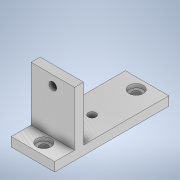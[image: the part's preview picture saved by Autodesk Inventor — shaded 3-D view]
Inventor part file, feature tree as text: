
AUTODESK INVENTOR PART (.ipt)
format: ipt  version: 2020 (Build 240168000, 168)  size: 157,696 bytes
history: native  units: mm
features: sketch x5, hole x3, extrude x2
ambient origin geometry x8: Origin, YZ Plane, XZ Plane, XY Plane, X Axis, Y Axis, Z Axis, Center Point
bodies: Body1 (feature_tree)
feature tree (10):
  extrude  "Extrusion8"  Depth=24.0mm
  hole  "Hole8"  [1 undecoded]
  extrude  "Extrusion10"  TaperAngle=0.0deg  [1 undecoded]
  hole  "Hole9"  [1 undecoded]
  hole  "Hole10"  [1 undecoded]
  sketch  "Sketch14"  dims[d93=28.0mm d94=24.0mm]
  sketch  "Sketch17"  dims[d95=16.0mm d96=5.0mm d97=0.0mm]
  sketch  "Sketch18"  dims[d111=19.0mm]
  sketch  "Sketch19"  dims[d112=4.305mm d113=6.0mm d114=7.938mm d115=2.0mm d116=14.3117mm d117=10.4mm d118=0.0mm d119=0.0mm]
  sketch  "Sketch20"  dims[d121=6.0mm d122=0.0mm d125=6.0mm d126=5.0mm d127=14.0mm d128=30.0mm d129=0.0mm d130=4.3mm d131=8.0mm d132=12.24mm d133=3.58mm d134=14.3117mm d135=11.8mm d136=0.0mm d138=24.659mm d139=4.3mm d140=8.0mm d141=8.0mm d142=2.0mm d143=14.3117mm d144=11.8mm d145=0.0mm d146=16.678mm d147=0.0mm d148=12.0mm]
note: 4 required parameter values undecoded (feature->parameter linkage not recoverable at this tier; creation-order binding heuristic only, values carry confidence <= 0.55)
